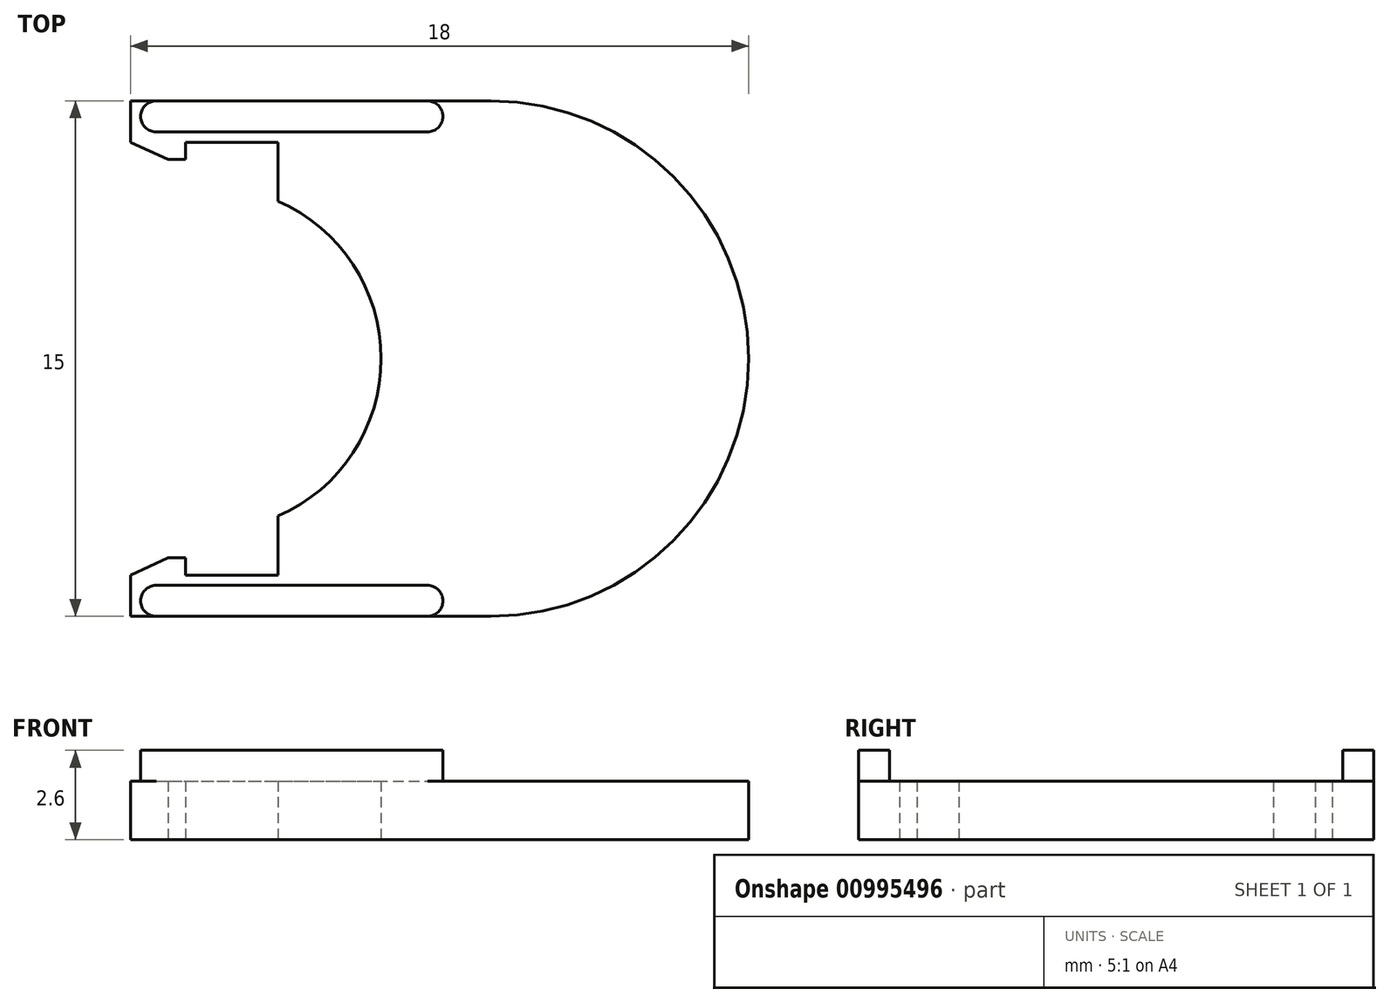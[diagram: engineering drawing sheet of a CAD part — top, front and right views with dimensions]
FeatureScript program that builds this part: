
annotation { "Feature Type Name" : "Feature", "Feature Type Description" : "" }
export const myFeature = defineFeature(function(context is Context, id is Id, definition is map)
    precondition{}
    {
        {
            var Q0;
            Q0=qCreatedBy(makeId("Top.planeOp"),FACE);
            var sketch = newSketch(context, id + "F0", { "sketchPlane" : qUnion([Q0])});
            skLineSegment(sketch, "E0.bottom", {"start": v(-9, 7.5) * mm, "end": v(1.5, 7.5) * mm});
            skLineSegment(sketch, "E0.top", {"start": v(-9, -7.5) * mm, "end": v(1.5, -7.5) * mm});
            skLineSegment(sketch, "E0.left", {"start": v(-9, 7.5) * mm, "end": v(-9, 6.3) * mm});
            skLineSegment(sketch, "E1.bottom", {"start": v(-7.4, -6.3) * mm, "end": v(-4.7, -6.3) * mm});
            skLineSegment(sketch, "E1.top", {"start": v(-7.4, 6.3) * mm, "end": v(-4.7, 6.3) * mm});
            skArc(sketch, "E2", {"start": v(1.5, -7.5) * mm, "mid": v(9, 0) * mm, "end": v(1.5, 7.5) * mm});
            skLineSegment(sketch, "E3.trimOffspring", {"start": v(-9, -6.3) * mm, "end": v(-9, -7.5) * mm});
            skLineSegment(sketch, "E4", {"start": v(-9, -6.3) * mm, "end": v(-7.9, -5.8) * mm});
            skLineSegment(sketch, "E5", {"start": v(-7.9, -5.8) * mm, "end": v(-7.4, -5.8) * mm});
            skLineSegment(sketch, "E6", {"start": v(-7.4, -5.8) * mm, "end": v(-7.4, -6.3) * mm});
            skLineSegment(sketch, "E7.MirrorCS", {"start": v(-9, 6.3) * mm, "end": v(-7.9, 5.8) * mm});
            skLineSegment(sketch, "E8.MirrorCS", {"start": v(-7.9, 5.8) * mm, "end": v(-7.4, 5.8) * mm});
            skLineSegment(sketch, "E9.MirrorCS", {"start": v(-7.4, 5.8) * mm, "end": v(-7.4, 6.3) * mm});
            skLineSegment(sketch, "E10.MirrorCS", {"start": v(-9, 6.3) * mm, "end": v(-9, 7.5) * mm});
            skLineSegment(sketch, "E11.left", {"start": v(-4.7, 6.3) * mm, "end": v(-4.7, 4.5) * mm});
            skLineSegment(sketch, "E12.trimOffspring", {"start": v(-4.7, 4.5) * mm, "end": v(-4.7, -6.3) * mm});
            skSolve(sketch);
        }
        {
            var Q0;
            Q0=qCreatedBy(makeId("Top.planeOp"),FACE);
            var sketch = newSketch(context, id + "F1", { "sketchPlane" : qUnion([Q0])});
            skArc(sketch, "E13", {"start": v(-4.7, -4.58) * mm, "mid": v(-1.7, 0) * mm, "end": v(-4.7, 4.58) * mm});
            skLineSegment(sketch, "E14.bottom", {"start": v(-13.7, 5.5) * mm, "end": v(-4.7, 5.5) * mm});
            skLineSegment(sketch, "E14.top", {"start": v(-13.7, -5.5) * mm, "end": v(-4.7, -5.5) * mm});
            skLineSegment(sketch, "E14.left", {"start": v(-4.7, 5.5) * mm, "end": v(-4.7, 4.58) * mm});
            skLineSegment(sketch, "E14.right", {"start": v(-13.7, 5.5) * mm, "end": v(-13.7, -5.5) * mm});
            skLineSegment(sketch, "E15.trimOffspring", {"start": v(-4.7, -4.58) * mm, "end": v(-4.7, -5.5) * mm});
            skSolve(sketch);
        }
        {
            var Q0;
            Q0=makeQuery(id+"F0.imprint","IMPRINT",FACE,{"disambiguationData":[TD([[makeQuery(id+"F0.imprint","IMPRINT",EDGE,{"derivedFrom":sQuery(id+"F0.wireOp",EDGE,"E0.bottom")}),-1.0]])]});
            extrude(context, id + "F2", {"entities" : qUnion([Q0]), "depth" : 1.7 * mm, "offsetDistance" : 25 * mm});
        }
        {
            var Q0;
            Q0 = qSketchRegion(id + "F1", true);
            extrude(context, id + "F3", {"entities" : qUnion([Q0]), "operationType" : NewBodyOperationType.REMOVE, "depth" : 2 * mm, "offsetDistance" : 25 * mm});
        }
        {
            var Q0;
            Q0=makeQuery(id+"F2.opExtrude","CAP_FACE",FACE,{"disambiguationData":[OSD([sQuery(id+"F0.wireOp",EDGE,"E0.bottom"),sQuery(id+"F0.wireOp",EDGE,"E0.top"),sQuery(id+"F0.wireOp",EDGE,"E1.bottom"),sQuery(id+"F0.wireOp",EDGE,"E2"),sQuery(id+"F0.wireOp",EDGE,"E3.trimOffspring"),sQuery(id+"F0.wireOp",EDGE,"E4"),sQuery(id+"F0.wireOp",EDGE,"E5"),sQuery(id+"F0.wireOp",EDGE,"E6"),sQuery(id+"F0.wireOp",EDGE,"E1.top"),sQuery(id+"F0.wireOp",EDGE,"E7.MirrorCS"),sQuery(id+"F0.wireOp",EDGE,"E9.MirrorCS"),sQuery(id+"F0.wireOp",EDGE,"E8.MirrorCS"),sQuery(id+"F0.wireOp",EDGE,"E10.MirrorCS"),sQuery(id+"F0.wireOp",EDGE,"E11.left"),sQuery(id+"F0.wireOp",EDGE,"E12.trimOffspring")])],"isStart":false});
            var sketch = newSketch(context, id + "F4", { "sketchPlane" : qUnion([Q0])});
            skLineSegment(sketch, "E16.bottom", {"start": v(-8.25, 7.5) * mm, "end": v(-0.35, 7.5) * mm});
            skLineSegment(sketch, "E16.top", {"start": v(-8.25, 6.6) * mm, "end": v(-0.35, 6.6) * mm});
            skArc(sketch, "E17", {"start": v(-8.25, 7.5) * mm, "mid": v(-8.7, 7.05) * mm, "end": v(-8.25, 6.6) * mm});
            skArc(sketch, "E18", {"start": v(-0.35, 6.6) * mm, "mid": v(0.1, 7.05) * mm, "end": v(-0.35, 7.5) * mm});
            skLineSegment(sketch, "E19.MirrorCS", {"start": v(-8.25, -6.6) * mm, "end": v(-0.35, -6.6) * mm});
            skArc(sketch, "E20.MirrorCS", {"start": v(-0.35, -6.6) * mm, "mid": v(0.1, -7.05) * mm, "end": v(-0.35, -7.5) * mm});
            skArc(sketch, "E21.MirrorCS", {"start": v(-8.25, -7.5) * mm, "mid": v(-8.7, -7.05) * mm, "end": v(-8.25, -6.6) * mm});
            skLineSegment(sketch, "E22.MirrorCS", {"start": v(-8.25, -7.5) * mm, "end": v(-0.35, -7.5) * mm});
            skSolve(sketch);
        }
        {
            var Q0;
            Q0 = qSketchRegion(id + "F4", true);
            extrude(context, id + "F5", {"entities" : qUnion([Q0]), "operationType" : NewBodyOperationType.ADD, "depth" : 0.9 * mm, "offsetDistance" : 25 * mm});
        }
    });
